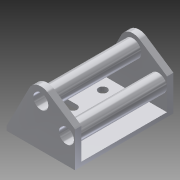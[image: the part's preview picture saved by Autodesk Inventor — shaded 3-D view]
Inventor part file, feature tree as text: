
AUTODESK INVENTOR PART (.ipt)
format: ipt  version: 2015 SP1 (Build 190203100, 203)  size: 290,816 bytes
history: native  units: in
note: dims shown in document units (in); Inventor stores cm internally (conversion verified against a paired STEP export)
features: extrude x7, sketch x7, projected_geometry x6
ambient origin geometry x8: Origin, YZ Plane, XZ Plane, XY Plane, X Axis, Y Axis, Z Axis, Center Point
bodies: Solid1 (feature_tree)
feature tree (20):
  extrude  "Extrusion1"  Depth=2.5in
  extrude  "Extrusion2"  Depth=2.0in
  extrude  "Extrusion3"  Depth=0.25in
  extrude  "Extrusion5"  Depth=0.25in
  extrude  "Extrusion6"  TaperAngle=0.0deg  [1 undecoded]
  extrude  "Extrusion7"  TaperAngle=0.0deg  [1 undecoded]
  extrude  "Extrusion8"  Depth=0.25in
  sketch  "Sketch1"  dims[d0=3.0in d1=2.5in]
  sketch  "Sketch2"  dims[d2=1.75in d3=2.0in]
  projected_geometry  "Projected Loop1"
  sketch  "Sketch3"  dims[d4=0.25in d5=0.25in]
  projected_geometry  "Projected Loop2"
  projected_geometry  "Projected Loop3"
  sketch  "Sketch5"  dims[d6=0.25in d7=0.5in]
  projected_geometry  "Projected Loop5"
  sketch  "Sketch6"  dims[d8=0.25in d9=0.0in]
  projected_geometry  "Projected Loop6"
  sketch  "Sketch7"  dims[d10=0.0in d11=0.0in]
  projected_geometry  "Projected Loop7"
  sketch  "Sketch8"  dims[d12=0.0in d13=0.25in d14=0.25in d15=0.5in d16=0.0in d17=0.25in d18=0.25in d19=0.0in d20=0.5in d21=0.125in d22=0.0in d23=0.4375in d24=1.25in d25=1.0in d26=0.4375in d27=0.75in d28=1.25in d29=0.375in d30=0.1875in d31=0.0in d32=0.1875in d33=0.0in d38=0.5in d39=0.5in d40=2.5in d41=0.0in d42=0.25in d43=0.25in d44=0.25in d45=0.25in d46=0.25in d47=0.25in d50=0.875in d51=0.875in d52=0.0in d53=0.0in d54=0.0in d55=0.5in d56=0.5in d57=0.0in d58=0.0in d59=0.0in d60=0.875in d61=0.875in d62=2.5in d63=0.0in d64=1.0in d65=3.25in d66=3.0in d67=2.5in d68=0.0in d69=2.5in d70=2.5in d71=1.0in d72=0.0in]
note: 2 required parameter values undecoded (feature->parameter linkage not recoverable at this tier; creation-order binding heuristic only, values carry confidence <= 0.55)
